# Revit family: FL3X-LEP_2014
name_source: partatom
category: Specialty Equipment
revit_build: Autodesk Revit 2014 (Build: 20130308_1515(x64)
units: mm (PartAtom-declared; Revit-internal decimal feet)

## types (1)
- 4'-0" Length
    Back Clearance = 3"
    Bumper = Extruded PVC - 733 Turquoise Blue
    Case = Textured Sheet Metal (Steel Painted) - 149 White Satin Matte
    Case Interior - Back Panel = Sheet Metal (Steel Painted) - 700 Interior White
    Case Interior - Side Panel = Sheet Metal (Steel Painted) - 700 Interior White
    Case Weight = 600.00 lbf
    Cutsheet URL = http://www.hussmann.com
    Depth = 42"
    Description = Floral, 3-Deck, Low Front, Extra High Energy Efficiency Coil
    End Weight = 75.00 lbf
    Ends = Textured Sheet Metal (Steel Painted) - 149 White Satin Matte
    Height = 63 1/8"
    Manufacturer = Hussmann Corporation
    Manufacturer Disclaimer = The information in this file is not intended to be an exact representation of the corresponding Hussmann product.  Further, we reserve the right to change or revise specifications and product design in connection with any feature of our products. Such changes do not entitle the buyer to corresponding changes, improvements, additions, or replacements for equipment previously sold or shipped.
    Model = FL3X-LEP
    Model URL = http://www.hussmann.com
    Note from Manufacturer = This model only comes only in 4'-0" length.
    Number of Shelves = 3
    Number of Supports = 2
    Refrigeration Lines Liquid = 3/8"
    Refrigeration Lines Suction = 7/8"
    Revit Family Date = 09/30/2016
    Shelves = Sheet Metal (Steel Painted) - 700 Interior White
    Splashguard = Textured Sheet Metal (Steel Painted) - 701 Black
    Top Clearance = 3"
    Total Weight = 750.00 lbf
    Trim = Stainless Steel
    Type Comments = Excel
    URL = www.hussmann.com
    Waste Drain = 1 1/4"
    Waste Drain Location = 12 1/8"
    Width = 48 3/8"

## geometry (parser evidence)
native form markers: Sweep x13
no freeform markers — native parametric forms only
